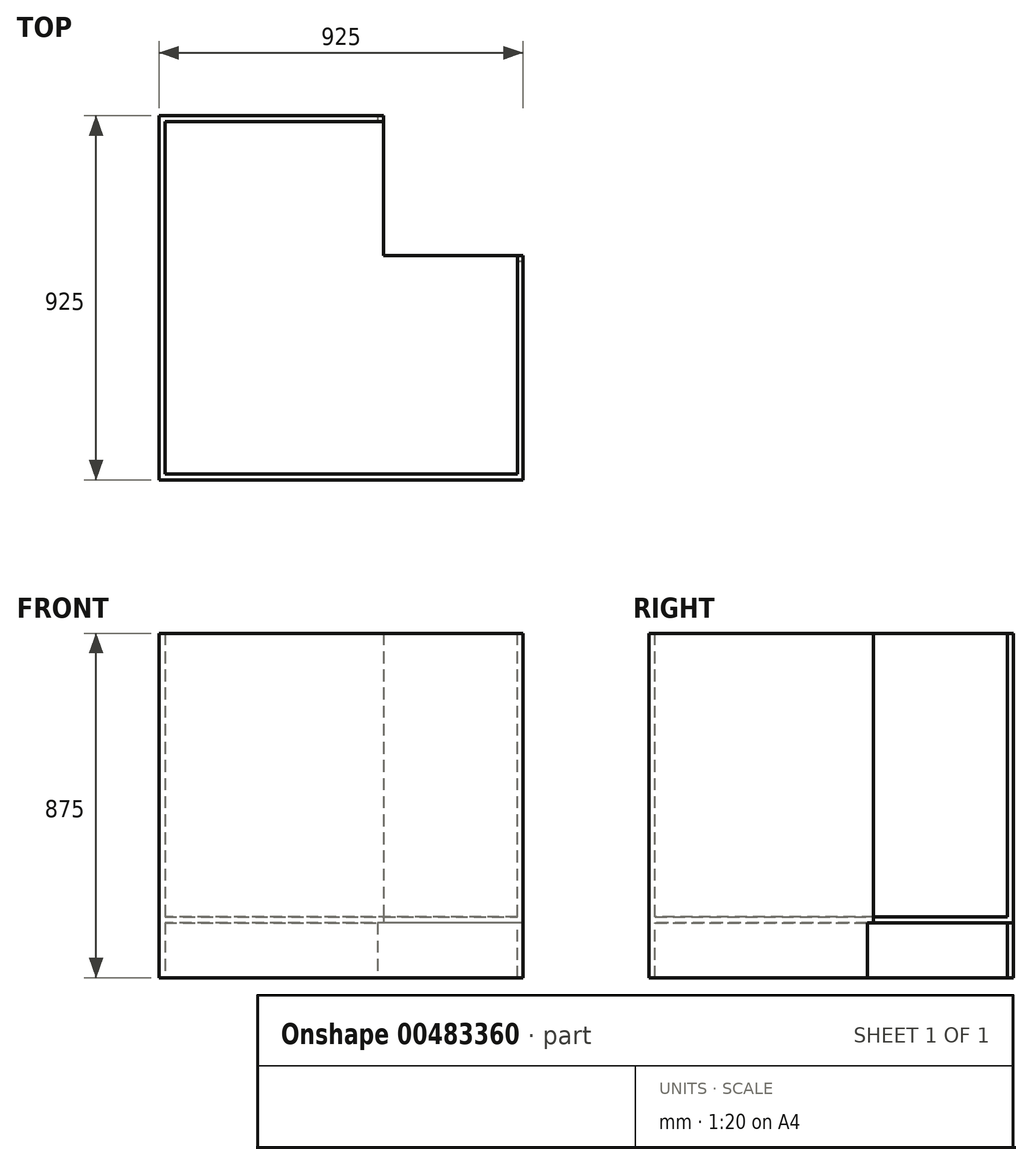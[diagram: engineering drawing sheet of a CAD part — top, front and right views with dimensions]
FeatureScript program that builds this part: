
annotation { "Feature Type Name" : "Feature", "Feature Type Description" : "" }
export const myFeature = defineFeature(function(context is Context, id is Id, definition is map)
    precondition{}
    {
        {
            var Q0;
            Q0=qCreatedBy(makeId("Right.planeOp"),FACE);
            var sketch = newSketch(context, id + "F0", { "sketchPlane" : qUnion([Q0])});
            skLineSegment(sketch, "E0", {"start": v(540, -140) * mm, "end": v(540, 0) * mm});
            skLineSegment(sketch, "E1", {"start": v(540, 0) * mm, "end": v(555, 0) * mm});
            skLineSegment(sketch, "E2", {"start": v(555, 0) * mm, "end": v(555, 735) * mm});
            skLineSegment(sketch, "E3", {"start": v(555, 735) * mm, "end": v(-15, 735) * mm});
            skLineSegment(sketch, "E4", {"start": v(-15, -140) * mm, "end": v(-15, 735) * mm});
            skLineSegment(sketch, "E5", {"start": v(-15, 735) * mm, "end": v(-15, 735) * mm});
            skLineSegment(sketch, "E6", {"start": v(-15, -140) * mm, "end": v(540, -140) * mm});
            skSolve(sketch);
        }
        {
            var Q0;
            Q0=qCreatedBy(makeId("Top.planeOp"),FACE);
            var sketch = newSketch(context, id + "F1", { "sketchPlane" : qUnion([Q0])});
            skLineSegment(sketch, "E7", {"start": v(0, 0) * mm, "end": v(-895, 0) * mm});
            skLineSegment(sketch, "E8", {"start": v(-895, 0) * mm, "end": v(-895, 895) * mm});
            skLineSegment(sketch, "E9", {"start": v(-895, 895) * mm, "end": v(-340, 895) * mm});
            skLineSegment(sketch, "E10", {"start": v(-340, 895) * mm, "end": v(-340, 555) * mm});
            skLineSegment(sketch, "E11", {"start": v(-340, 555) * mm, "end": v(0, 555) * mm});
            skLineSegment(sketch, "E12", {"start": v(0, 555) * mm, "end": v(0, 0) * mm});
            skSolve(sketch);
        }
        {
            var Q0;
            Q0 = qSketchRegion(id + "F0", true);
            extrude(context, id + "F2", {"entities" : qUnion([Q0]), "depth" : 15 * mm});
        }
        {
            var Q0;
            Q0=makeQuery(id+"F1.imprint","IMPRINT",FACE,{"disambiguationData":[TD([[makeQuery(id+"F1.imprint","IMPRINT",EDGE,{"derivedFrom":sQuery(id+"F1.wireOp",EDGE,"E7")}),-1.0]])]});
            extrude(context, id + "F3", {"entities" : qUnion([Q0]), "operationType" : NewBodyOperationType.ADD, "depth" : 15 * mm});
        }
        {
            var Q0;
            Q0=makeQuery(id+"F3.opExtrude","SWEPT_FACE",FACE,{"disambiguationData":[OSD([sQuery(id+"F1.wireOp",EDGE,"E8")])]});
            cPlane(context, id + "F4", {"entities" : qUnion([Q0]), "cplaneType" : CPlaneType.OFFSET, "offset" : 0 * mm, "width" : 150 * mm, "height" : 150 * mm});
        }
        {
            var Q0;
            Q0=qCreatedBy(id+"F4.planeOp",FACE);
            var sketch = newSketch(context, id + "F5", { "sketchPlane" : qUnion([Q0])});
            skLineSegment(sketch, "E13", {"start": v(0, 0) * mm, "end": v(0, -140) * mm});
            skLineSegment(sketch, "E14", {"start": v(0, -140) * mm, "end": v(-895, -140) * mm});
            skLineSegment(sketch, "E15", {"start": v(-895, -140) * mm, "end": v(-895, 735) * mm});
            skLineSegment(sketch, "E16", {"start": v(-895, 735) * mm, "end": v(0, 735) * mm});
            skLineSegment(sketch, "E17", {"start": v(0, 735) * mm, "end": v(0, 0) * mm});
            skSolve(sketch);
        }
        {
            var Q0;
            Q0=makeQuery(id+"F5.imprint","IMPRINT",FACE,{"disambiguationData":[TD([[makeQuery(id+"F5.imprint","IMPRINT",EDGE,{"derivedFrom":sQuery(id+"F5.wireOp",EDGE,"E13")}),-1.0]])]});
            extrude(context, id + "F6", {"entities" : qUnion([Q0]), "operationType" : NewBodyOperationType.ADD, "depth" : 15 * mm});
        }
        {
            var Q0;
            Q0=makeQuery(id+"F6.boolean.opBoolean","MERGE",FACE,{"derivedFrom":[makeQuery(id+"F3.opExtrude","SWEPT_FACE",FACE,{"disambiguationData":[OSD([sQuery(id+"F1.wireOp",EDGE,"E9")])]}),makeQuery(id+"F6.opExtrude","SWEPT_FACE",FACE,{"disambiguationData":[OSD([sQuery(id+"F5.wireOp",EDGE,"E15")])]})]});
            cPlane(context, id + "F7", {"entities" : qUnion([Q0]), "cplaneType" : CPlaneType.OFFSET, "offset" : 0 * mm, "width" : 150 * mm, "height" : 150 * mm});
        }
        {
            var Q0;
            Q0=qCreatedBy(id+"F7.planeOp",FACE);
            var sketch = newSketch(context, id + "F8", { "sketchPlane" : qUnion([Q0])});
            skLineSegment(sketch, "E18.0", {"start": v(910, -140) * mm, "end": v(910, 735) * mm});
            skLineSegment(sketch, "E19", {"start": v(910, 735) * mm, "end": v(340, 735) * mm});
            skLineSegment(sketch, "E20", {"start": v(340, 735) * mm, "end": v(340, 0) * mm});
            skLineSegment(sketch, "E21", {"start": v(340, 0) * mm, "end": v(355, 0) * mm});
            skLineSegment(sketch, "E22", {"start": v(355, 0) * mm, "end": v(355, -140) * mm});
            skLineSegment(sketch, "E23", {"start": v(355, -140) * mm, "end": v(910, -140) * mm});
            skSolve(sketch);
        }
        {
            var Q0;
            Q0=makeQuery(id+"F8.imprint","IMPRINT",FACE,{"disambiguationData":[TD([[makeQuery(id+"F8.imprint","IMPRINT",EDGE,{"derivedFrom":sQuery(id+"F8.wireOp",EDGE,"E18.0")}),1.0]])]});
            extrude(context, id + "F9", {"entities" : qUnion([Q0]), "operationType" : NewBodyOperationType.ADD, "depth" : 15 * mm});
        }
        {
            var Q0;
            Q0=makeQuery(id+"F6.boolean.opBoolean","MERGE",FACE,{"derivedFrom":[makeQuery(id+"F3.opExtrude","SWEPT_FACE",FACE,{"disambiguationData":[OSD([sQuery(id+"F1.wireOp",EDGE,"E7")])]}),makeQuery(id+"F6.opExtrude","SWEPT_FACE",FACE,{"disambiguationData":[OSD([sQuery(id+"F5.wireOp",EDGE,"E13"),sQuery(id+"F5.wireOp",EDGE,"E17")])]})]});
            cPlane(context, id + "F10", {"entities" : qUnion([Q0]), "cplaneType" : CPlaneType.OFFSET, "offset" : 0 * mm, "width" : 150 * mm, "height" : 150 * mm});
        }
        {
            var Q0;
            Q0=qCreatedBy(id+"F10.planeOp",FACE);
            var sketch = newSketch(context, id + "F11", { "sketchPlane" : qUnion([Q0])});
            skLineSegment(sketch, "E24.0", {"start": v(-910, 735) * mm, "end": v(-910, -140) * mm});
            skLineSegment(sketch, "E25", {"start": v(-910, -140) * mm, "end": v(0, -140) * mm});
            skLineSegment(sketch, "E26", {"start": v(0, -140) * mm, "end": v(0, 735) * mm});
            skLineSegment(sketch, "E27", {"start": v(0, 735) * mm, "end": v(-910, 735) * mm});
            skSolve(sketch);
        }
        {
            var Q0;
            Q0=makeQuery(id+"F11.imprint","IMPRINT",FACE,{"disambiguationData":[TD([[makeQuery(id+"F11.imprint","IMPRINT",EDGE,{"derivedFrom":sQuery(id+"F11.wireOp",EDGE,"E24.0")}),1.0]])]});
            extrude(context, id + "F12", {"entities" : qUnion([Q0]), "operationType" : NewBodyOperationType.ADD, "depth" : 15 * mm});
        }
    });
